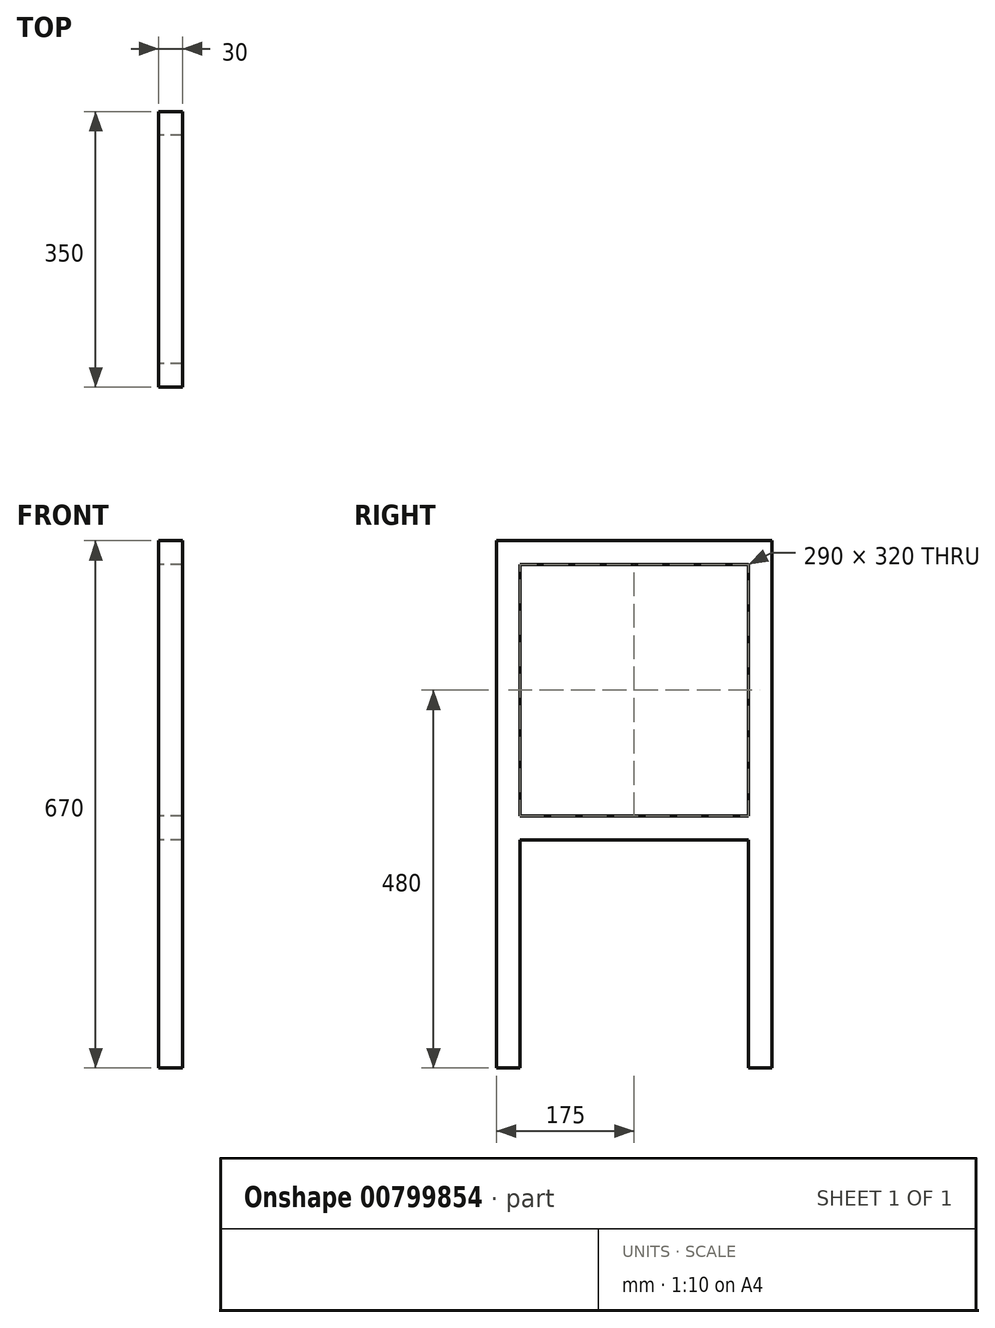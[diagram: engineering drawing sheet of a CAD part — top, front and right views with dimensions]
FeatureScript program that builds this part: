
annotation { "Feature Type Name" : "Feature", "Feature Type Description" : "" }
export const myFeature = defineFeature(function(context is Context, id is Id, definition is map)
    precondition{}
    {
        {
            var Q0;
            Q0=qCreatedBy(makeId("Right.planeOp"),FACE);
            var sketch = newSketch(context, id + "F0", { "sketchPlane" : qUnion([Q0])});
            skLineSegment(sketch, "E0.bottom", {"start": v(-320, -350) * mm, "end": v(-30, -350) * mm});
            skLineSegment(sketch, "E0.top", {"start": v(-320, -30) * mm, "end": v(-30, -30) * mm});
            skLineSegment(sketch, "E0.left", {"start": v(-320, -350) * mm, "end": v(-320, -30) * mm});
            skLineSegment(sketch, "E0.right", {"start": v(-30, -350) * mm, "end": v(-30, -30) * mm});
            skPoint(sketch, "E0.middle", {"position": v(-175, -190) * mm});
            skLineSegment(sketch, "E1", {"start": v(0, 0) * mm, "end": v(0, -670) * mm});
            skLineSegment(sketch, "E2", {"start": v(0, -670) * mm, "end": v(-30, -670) * mm});
            skLineSegment(sketch, "E3", {"start": v(-30, -670) * mm, "end": v(-30, -380) * mm});
            skLineSegment(sketch, "E4", {"start": v(-30, -380) * mm, "end": v(-320, -380) * mm});
            skLineSegment(sketch, "E5", {"start": v(-320, -380) * mm, "end": v(-320, -670) * mm});
            skLineSegment(sketch, "E6", {"start": v(-320, -670) * mm, "end": v(-350, -670) * mm});
            skLineSegment(sketch, "E7", {"start": v(-350, -670) * mm, "end": v(-350, 0) * mm});
            skLineSegment(sketch, "E8", {"start": v(-350, 0) * mm, "end": v(0, 0) * mm});
            skSolve(sketch);
        }
        {
            var Q0;
            Q0=makeQuery(id+"F0.imprint","IMPRINT",FACE,{"disambiguationData":[TD([[makeQuery(id+"F0.imprint","IMPRINT",EDGE,{"derivedFrom":sQuery(id+"F0.wireOp",EDGE,"E0.bottom")}),-1.0]])]});
            extrude(context, id + "F1", {"entities" : qUnion([Q0]), "depth" : 30 * mm, "offsetDistance" : 25 * mm});
        }
    });
